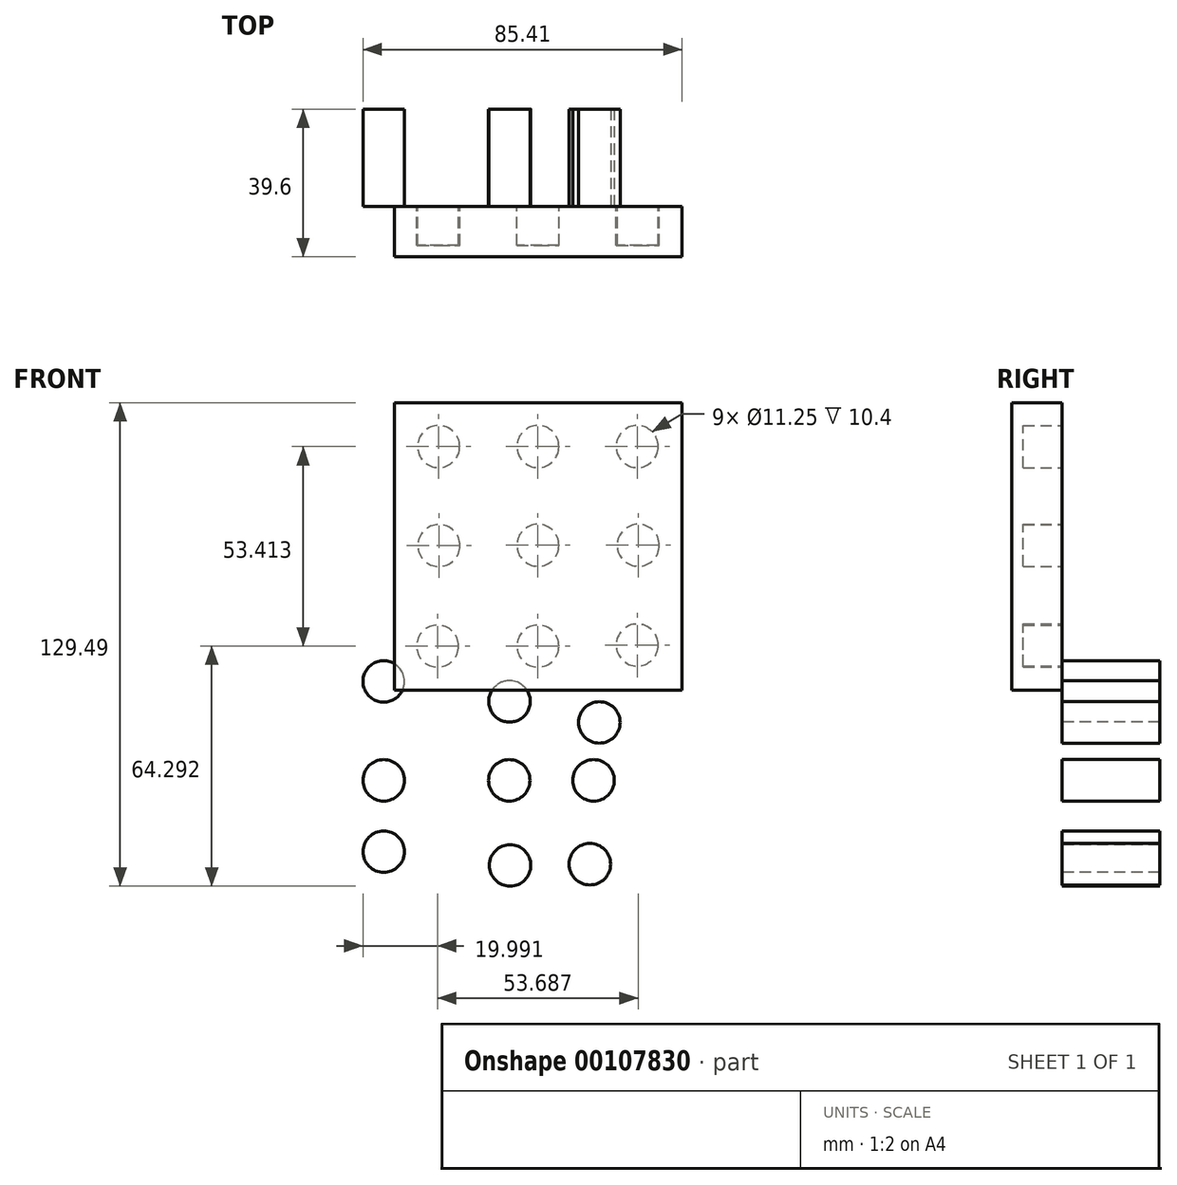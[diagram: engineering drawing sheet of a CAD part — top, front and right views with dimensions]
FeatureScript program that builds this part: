
annotation { "Feature Type Name" : "Feature", "Feature Type Description" : "" }
export const myFeature = defineFeature(function(context is Context, id is Id, definition is map)
    precondition{}
    {
        {
            var Q0;
            Q0=qCreatedBy(makeId("Front.planeOp"),FACE);
            var sketch = newSketch(context, id + "F0", { "sketchPlane" : qUnion([Q0])});
            skLineSegment(sketch, "E0.bottom", {"start": v(-59.79, 55.2) * mm, "end": v(17.21, 55.2) * mm});
            skLineSegment(sketch, "E0.top", {"start": v(-59.79, -21.8) * mm, "end": v(17.21, -21.8) * mm});
            skLineSegment(sketch, "E0.left", {"start": v(-59.79, 55.2) * mm, "end": v(-59.79, -21.8) * mm});
            skLineSegment(sketch, "E0.right", {"start": v(17.21, 55.2) * mm, "end": v(17.21, -21.8) * mm});
            skLineSegment(sketch, "E1", {"start": v(-59.79, 62.2) * mm, "end": v(17.21, 62.2) * mm, "construction": true});
            skPoint(sketch, "E2", {"position": v(-21.29, 62.2) * mm});
            skLineSegment(sketch, "E3", {"start": v(-21.29, 62.2) * mm, "end": v(-21.29, -32.7) * mm, "construction": true});
            skPoint(sketch, "E3.endSnap0", {"position": v(-21.29, -21.8) * mm});
            skLineSegment(sketch, "E4", {"start": v(-21.29, 14.75) * mm, "end": v(-59.79, 14.75) * mm, "construction": true});
            skLineSegment(sketch, "E5", {"start": v(-21.29, 14.75) * mm, "end": v(17.21, 14.75) * mm, "construction": true});
            skLineSegment(sketch, "E6", {"start": v(-47.91, 62.2) * mm, "end": v(-47.91, -31.86) * mm, "construction": true});
            skLineSegment(sketch, "E7", {"start": v(5.34, 62.2) * mm, "end": v(5.34, -35.76) * mm, "construction": true});
            skLineSegment(sketch, "E8", {"start": v(20.87, 43.32) * mm, "end": v(-63.45, 43.32) * mm, "construction": true});
            skLineSegment(sketch, "E9", {"start": v(-62.9, -9.93) * mm, "end": v(23.66, -9.93) * mm, "construction": true});
            skSolve(sketch);
        }
        {
            var Q0;
            Q0=makeQuery(id+"F0.imprint","IMPRINT",FACE,{"disambiguationData":[TD([[makeQuery(id+"F0.imprint","IMPRINT",EDGE,{"derivedFrom":sQuery(id+"F0.wireOp",EDGE,"E0.bottom")}),-1.0]])]});
            extrude(context, id + "F1", {"entities" : qUnion([Q0]), "depth" : 13.5 * mm});
        }
        {
            var Q0;
            Q0=qCreatedBy(makeId("Front.planeOp"),FACE);
            var sketch = newSketch(context, id + "F2", { "sketchPlane" : qUnion([Q0])});
            skCircle(sketch, "E10", {"center": v(-47.93, 43.42) * mm, "radius": 5.62 * mm});
            skCircle(sketch, "E11", {"center": v(-47.87, 16.9) * mm, "radius": 5.62 * mm});
            skCircle(sketch, "E12", {"center": v(-48.2, -10) * mm, "radius": 5.62 * mm});
            skLineSegment(sketch, "E13", {"start": v(-63.27, 43.69) * mm, "end": v(-63.27, -9.72) * mm, "construction": true});
            skLineSegment(sketch, "E14", {"start": v(-63.27, 16.98) * mm, "end": v(26.84, 16.98) * mm, "construction": true});
            skCircle(sketch, "E15", {"center": v(-21.37, 43.42) * mm, "radius": 5.62 * mm});
            skCircle(sketch, "E16", {"center": v(-21.37, 16.98) * mm, "radius": 5.62 * mm});
            skCircle(sketch, "E17", {"center": v(-21.37, -10) * mm, "radius": 5.62 * mm});
            skCircle(sketch, "E18", {"center": v(5.2, 43.42) * mm, "radius": 5.62 * mm});
            skCircle(sketch, "E19", {"center": v(5.48, 16.98) * mm, "radius": 5.62 * mm});
            skCircle(sketch, "E20", {"center": v(5.2, -9.72) * mm, "radius": 5.62 * mm});
            skSolve(sketch);
        }
        {
            var Q0;
            Q0 = qSketchRegion(id + "F2", true);
            extrude(context, id + "F3", {"entities" : qUnion([Q0]), "operationType" : NewBodyOperationType.REMOVE, "depth" : 10.4 * mm});
        }
        {
            var Q0;
            Q0=qCreatedBy(makeId("Front.planeOp"),FACE);
            var sketch = newSketch(context, id + "F4", { "sketchPlane" : qUnion([Q0])});
            skCircle(sketch, "E21", {"center": v(5.23, 43.5) * mm, "radius": 5.55 * mm});
            skSolve(sketch);
        }
        {
            var Q0;
            Q0=makeQuery(id+"F4.imprint","IMPRINT",FACE,{"disambiguationData":[TD([[makeQuery(id+"F4.imprint","IMPRINT",EDGE,{"derivedFrom":sQuery(id+"F4.wireOp",EDGE,"E21")}),1.0]])]});
            var Q1;
            Q1=sQuery(id+"F4.wireOp",EDGE,"E21");
            extrude(context, id + "F5", {"entities" : qUnion([Q0]), "surfaceEntities" : qUnion([Q1]), "depth" : 26.95 * mm});
        }
        {
            var Q0;
            Q0=makeQuery(id+"F5.opExtrude","SWEPT_BODY",BODY,{"disambiguationData":[OSD([sQuery(id+"F4.wireOp",EDGE,"E21")])]});
            deleteBodies(context, id + "F6", {"entities" : qUnion([Q0])});
        }
        {
            var Q0;
            Q0=qCreatedBy(makeId("Front.planeOp"),FACE);
            var sketch = newSketch(context, id + "F7", { "sketchPlane" : qUnion([Q0])});
            skCircle(sketch, "E22", {"center": v(-62.65, -45.96) * mm, "radius": 5.55 * mm});
            skSolve(sketch);
        }
        {
            var Q0;
            Q0=makeQuery(id+"F7.imprint","IMPRINT",FACE,{"disambiguationData":[TD([[makeQuery(id+"F7.imprint","IMPRINT",EDGE,{"derivedFrom":sQuery(id+"F7.wireOp",EDGE,"E22")}),1.0]])]});
            extrude(context, id + "F8", {"entities" : qUnion([Q0]), "oppositeDirection" : true, "depth" : 26.1 * mm});
        }
        {
            var Q0;
            Q0=makeQuery(id+"F8.opExtrude","SWEPT_BODY",BODY,{"disambiguationData":[OSD([sQuery(id+"F7.wireOp",EDGE,"E22")])]});
            transform(context, id + "F9", {"entities" : qUnion([Q0]), "transformType" : TransformType.TRANSLATION_3D, "dx" : 33.67 * mm, "dy" : 0 * mm, "dz" : 21.13 * mm, "makeCopy" : true});
        }
        {
            var Q0;
            Q0=makeQuery(id+"F8.opExtrude","SWEPT_BODY",BODY,{"disambiguationData":[OSD([sQuery(id+"F7.wireOp",EDGE,"E22")])]});
            transform(context, id + "F10", {"entities" : qUnion([Q0]), "transformType" : TransformType.TRANSLATION_3D, "dx" : 33.6 * mm, "dy" : 0 * mm, "dz" : 0 * mm, "makeCopy" : true});
        }
        {
            var Q0;
            Q0=makeQuery(id+"F8.opExtrude","SWEPT_BODY",BODY,{"disambiguationData":[OSD([sQuery(id+"F7.wireOp",EDGE,"E22")])]});
            transform(context, id + "F11", {"entities" : qUnion([Q0]), "transformType" : TransformType.TRANSLATION_3D, "dx" : 0 * mm, "dy" : 0 * mm, "dz" : 26.48 * mm, "makeCopy" : true});
        }
        {
            var Q0;
            Q0=makeQuery(id+"F8.opExtrude","SWEPT_BODY",BODY,{"disambiguationData":[OSD([sQuery(id+"F7.wireOp",EDGE,"E22")])]});
            transform(context, id + "F12", {"entities" : qUnion([Q0]), "transformType" : TransformType.TRANSLATION_3D, "dx" : 56.18 * mm, "dy" : 0 * mm, "dz" : 0 * mm, "makeCopy" : true});
        }
        {
            var Q0;
            Q0=makeQuery(id+"F8.opExtrude","SWEPT_BODY",BODY,{"disambiguationData":[OSD([sQuery(id+"F7.wireOp",EDGE,"E22")])]});
            transform(context, id + "F13", {"entities" : qUnion([Q0]), "transformType" : TransformType.TRANSLATION_3D, "dx" : 57.72 * mm, "dy" : 0 * mm, "dz" : 15.5 * mm, "makeCopy" : true});
        }
        {
            var Q0;
            Q0=makeQuery(id+"F8.opExtrude","SWEPT_BODY",BODY,{"disambiguationData":[OSD([sQuery(id+"F7.wireOp",EDGE,"E22")])]});
            transform(context, id + "F14", {"entities" : qUnion([Q0]), "transformType" : TransformType.TRANSLATION_3D, "dx" : 0 * mm, "dy" : 0 * mm, "dz" : -19.1 * mm, "makeCopy" : true});
        }
        {
            var Q0;
            Q0=makeQuery(id+"F8.opExtrude","SWEPT_BODY",BODY,{"disambiguationData":[OSD([sQuery(id+"F7.wireOp",EDGE,"E22")])]});
            transform(context, id + "F15", {"entities" : qUnion([Q0]), "transformType" : TransformType.TRANSLATION_3D, "dx" : 55.18 * mm, "dy" : 0 * mm, "dz" : -22.46 * mm, "makeCopy" : true});
        }
        {
            var Q0;
            Q0=makeQuery(id+"F8.opExtrude","SWEPT_BODY",BODY,{"disambiguationData":[OSD([sQuery(id+"F7.wireOp",EDGE,"E22")])]});
            transform(context, id + "F16", {"entities" : qUnion([Q0]), "transformType" : TransformType.TRANSLATION_3D, "dx" : 33.83 * mm, "dy" : 0 * mm, "dz" : -22.78 * mm, "makeCopy" : true});
        }
    });
